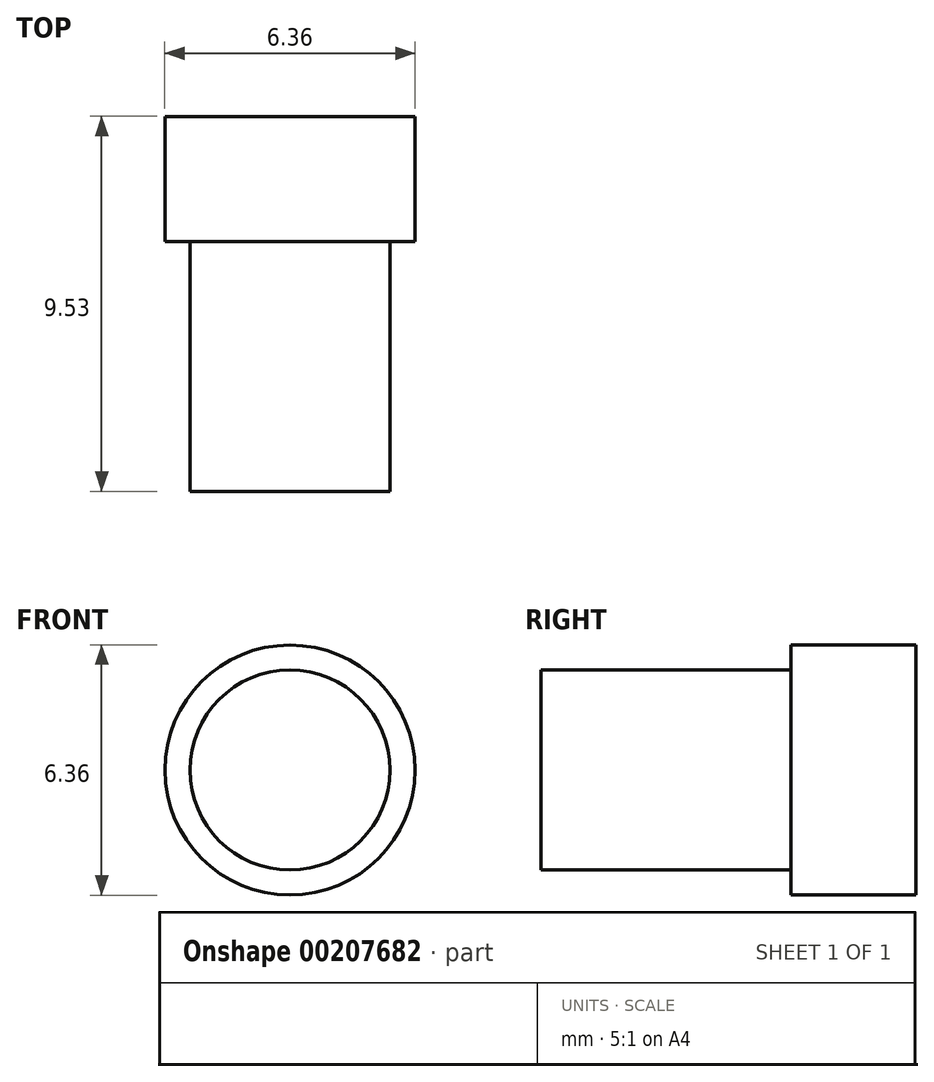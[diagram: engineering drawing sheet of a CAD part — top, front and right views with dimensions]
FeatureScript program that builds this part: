
annotation { "Feature Type Name" : "Feature", "Feature Type Description" : "" }
export const myFeature = defineFeature(function(context is Context, id is Id, definition is map)
    precondition{}
    {
        {
            var Q0;
            Q0=qCreatedBy(makeId("Front.planeOp"),FACE);
            var sketch = newSketch(context, id + "F0", { "sketchPlane" : qUnion([Q0])});
            skCircle(sketch, "E0", {"center": v(0, 0) * mm, "radius": 3.18 * mm});
            skSolve(sketch);
        }
        {
            var Q0;
            Q0 = qSketchRegion(id + "F0", true);
            extrude(context, id + "F1", {"entities" : qUnion([Q0]), "depth" : 6.35 * mm});
        }
        {
            var Q0;
            Q0=makeQuery(id+"F1.opExtrude","CAP_FACE",FACE,{"disambiguationData":[OSD([sQuery(id+"F0.wireOp",EDGE,"E0")])],"isStart":false});
            var sketch = newSketch(context, id + "F2", { "sketchPlane" : qUnion([Q0])});
            skCircle(sketch, "E1", {"center": v(0, 0) * mm, "radius": 2.54 * mm});
            skSolve(sketch);
        }
        {
            var Q0;
            Q0 = qSketchRegion(id + "F2", true);
            extrude(context, id + "F3", {"entities" : qUnion([Q0]), "operationType" : NewBodyOperationType.ADD, "depth" : 6.35 * mm, "hasSecondDirection" : true, "secondDirectionOppositeDirection" : true, "secondDirectionDepth" : 12.7 * mm});
        }
        {
            var Q0;
            Q0=qCreatedBy(makeId("Right.planeOp"),FACE);
            var sketch = newSketch(context, id + "F4", { "sketchPlane" : qUnion([Q0])});
            skLineSegment(sketch, "E2", {"start": v(0, 0) * mm, "end": v(-3.18, 0) * mm});
            skLineSegment(sketch, "E3", {"start": v(-3.18, 3.87) * mm, "end": v(-3.18, -4.04) * mm});
            skLineSegment(sketch, "E4", {"start": v(-3.18, -4.04) * mm, "end": v(8.1, -4.04) * mm});
            skLineSegment(sketch, "E5", {"start": v(8.1, -4.04) * mm, "end": v(8.1, 3.65) * mm});
            skLineSegment(sketch, "E6", {"start": v(8.1, 3.65) * mm, "end": v(-3.18, 3.87) * mm});
            skSolve(sketch);
        }
        {
            var Q0;
            {var subQ2=sQuery(id+"F4.wireOp",EDGE,"E4");Q0=makeQuery(id+"F4.imprint","IMPRINT",FACE,{"disambiguationData":[TD([[makeQuery(id+"F4.imprint","IMPRINT",EDGE,{"derivedFrom":subQ2}),1.0]])]});}
            extrude(context, id + "F5", {"entities" : qUnion([Q0]), "operationType" : NewBodyOperationType.REMOVE, "oppositeDirection" : true, "depth" : 12.7 * mm});
        }
        {
            var Q0;
            Q0=makeQuery(id+"F5.boolean.opBoolean","COPY",FACE,{"derivedFrom":makeQuery(id+"F5.opExtrude","CAP_FACE",FACE,{"disambiguationData":[OSD([sQuery(id+"F4.wireOp",EDGE,"E3"),sQuery(id+"F4.wireOp",EDGE,"E4"),sQuery(id+"F4.wireOp",EDGE,"E5"),sQuery(id+"F4.wireOp",EDGE,"E6")])],"isStart":true})});
            var sketch = newSketch(context, id + "F6", { "sketchPlane" : qUnion([Q0])});
            skLineSegment(sketch, "E7", {"start": v(3.18, 3.17) * mm, "end": v(-7.2, 3.17) * mm});
            skLineSegment(sketch, "E8", {"start": v(-7.2, 3.17) * mm, "end": v(-7.2, -3.17) * mm});
            skLineSegment(sketch, "E9", {"start": v(-7.2, -3.17) * mm, "end": v(3.18, -3.17) * mm});
            skLineSegment(sketch, "E10", {"start": v(3.18, -3.17) * mm, "end": v(3.18, 3.17) * mm});
            skSolve(sketch);
        }
        {
            var Q0;
            Q0 = qSketchRegion(id + "F6", true);
            extrude(context, id + "F7", {"entities" : qUnion([Q0]), "operationType" : NewBodyOperationType.REMOVE, "oppositeDirection" : true, "depth" : 25.4 * mm});
        }
    });
